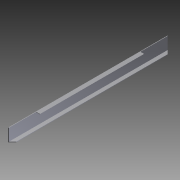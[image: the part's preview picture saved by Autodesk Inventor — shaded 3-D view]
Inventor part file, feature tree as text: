
AUTODESK INVENTOR PART (.ipt)
format: ipt  version: 2012 (Build 160160000, 160)  size: 98,304 bytes
history: native  units: in
note: dims shown in document units (in); Inventor stores cm internally (conversion verified against a paired STEP export)
features: extrude x3, sketch x2
ambient origin geometry x8: Origin, YZ Plane, XZ Plane, XY Plane, X Axis, Y Axis, Z Axis, Center Point
bodies: Solid1 (feature_tree)
feature tree (5):
  extrude  "Extrusion1"  Depth=1.0in
  sketch  "Sketch2"  dims[d2=0.125in d3=0.125in d4=0.125in d5=38.0in d6=0.0in d7=45.0deg d8=0.125in d9=6.5in d10=6.5in d11=28.0in d12=0.0in d13=28.0in d14=0.0in]
  extrude  "Extrusion2"  Depth=0.125in
  extrude  "Extrusion3"  Depth=0.125in
  sketch  "Sketch1"  dims[d0=3.0in d1=1.0in]
